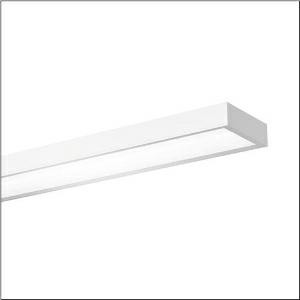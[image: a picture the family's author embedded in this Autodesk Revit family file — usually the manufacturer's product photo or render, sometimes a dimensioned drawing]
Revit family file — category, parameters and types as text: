
# Revit family: sport_31_51hs12dc3dca
name_source: partatom
category: Lighting Fixtures
units: mm (PartAtom-declared; Revit-internal decimal feet)

## family parameters
Cut with Voids When Loaded = No
Host = Face
Light Source = No
Part Type = Normal
Room Calculation Point = No
Round Connector Dimension = Use Diameter
Shared = No

## types (1)
- --- (1 x LED, 7500 lm, 55.4 W, 3000K)
    Apparent Load = 55 VA
    CIE Flux Codes = 65 89 97 100 100
    Color Rendering = 80
    Color Temperature = 3000K
    Default Elevation = 1800 mm
    Description = Sport 31, high bay luminaire, primary light control with reflector, of sheet steel, primary anti-glare with prismatic structure, of PC, primary optical cover: cover panel, of PC, light emission: direct distribution, primary light characteristic: symmetric, installation type: suspended mounting, recessed, surface-mounted, LED, rated luminous flux: 7.500lm, luminous efficacy: 130lm/W, light colour: 830, colour temperature: 3000K, control gear: DALI 2, with terminal, 5-pole, max. 2.5mm², mains connection: 220..240V, AC/DC, 50/60Hz, rated input power: 58W, housing, of sheet steel, traffic white (RAL 9016), length: 1.540mm, width: 315mm, height: 95mm, protection rating (complete): IP20, protection rating (lamp compartment, on room side): IP50, insulation class (complete): insulation class I (protective earthing), certification: CE, ENEC, UKCA, ball protection: ball impact resistant with ceiling mounting or chain suspension, impact resistance: IK08, permissible operating ambient temperature: -20..+35°C, standard: DIN 18032-3, EN 60598-2-22, packaging unit: 1 piece
    Height = 100 mm  [stored 0.328084 ft]
    Lamp = 1 x LED
    Lamp Light Flux = 7500 lm
    Lamp Power = 55.4 W
    Lamp count = 1
    Length = 1500 mm
    Luminous efficacy = 135 lm/W
    Manufacturer = Siteco
    ModVariant = No
    Model = 51HS12DC3DCA
    Mounting Place = Ceiling
    Mounting Type = Pendant
    Number of Poles = 1
    OnlyDefault = Yes
    Power Factor = 1
    Product Name = Sport 31
    Product group = high bay luminaire
    ProductGroupID = 901
    Protection Class = Protection class I
    Protection Degree = IP 20
    RLX_Detail_Level = 1
    RLX_Emergency_Light_Flux = 0 lm
    RLX_Emergency_Type = 0
    RLX_Emergency_Type_DB = No
    RlxData = <blob elided: 22761 chars, md5=355e383f>
    Socket = socket
    Standby Power = 0 W
    System Light Flux = 7500 lm
    System Power = 55 W
    Type Comments = factory setting: luminous flux: 100 % | dim-lin: 254 | 234 mA
    Type Image = l_1006823.jpg
    URL = http://relux.com
    VarID = @adj_218559
    Voltage = 0 V
    Weight = 0.00 kg
    Width = 315 mm

note: [stored X ft] marks values corroborated as IEEE doubles in the binary element streams (Revit-internal decimal feet)

## geometry (parser evidence)
native form markers: Blend x4, Sweep x11
no freeform markers — native parametric forms only
